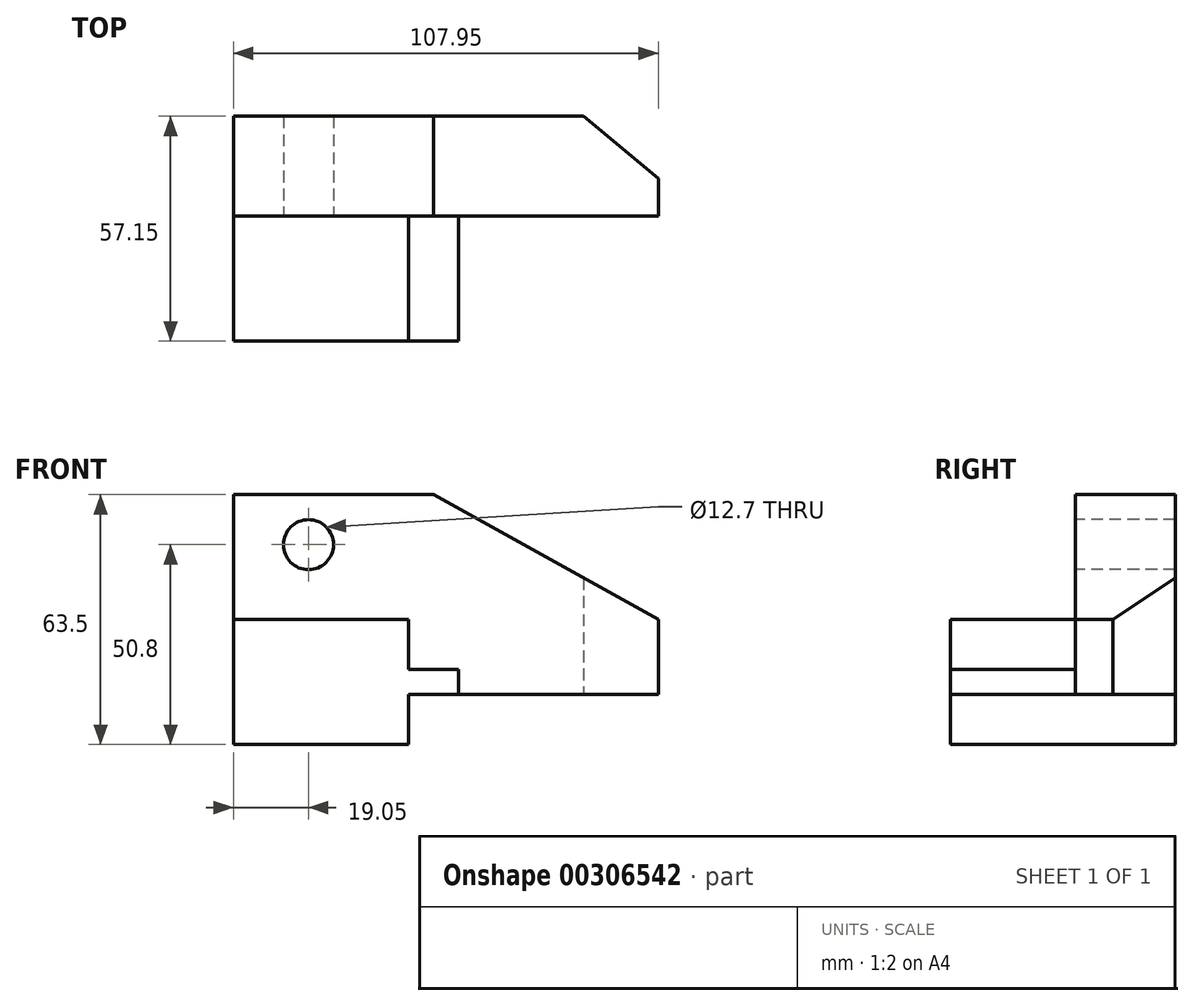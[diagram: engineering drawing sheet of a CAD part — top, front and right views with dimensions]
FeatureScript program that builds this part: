
annotation { "Feature Type Name" : "Feature", "Feature Type Description" : "" }
export const myFeature = defineFeature(function(context is Context, id is Id, definition is map)
    precondition{}
    {
        {
            var Q0;
            Q0=qCreatedBy(makeId("Front.planeOp"),FACE);
            var sketch = newSketch(context, id + "F0", { "sketchPlane" : qUnion([Q0])});
            skLineSegment(sketch, "E0.bottom", {"start": v(0, 0) * mm, "end": v(107.95, 0) * mm});
            skLineSegment(sketch, "E0.top", {"start": v(0, 63.5) * mm, "end": v(107.95, 63.5) * mm});
            skLineSegment(sketch, "E0.left", {"start": v(0, 0) * mm, "end": v(0, 63.5) * mm});
            skLineSegment(sketch, "E0.right", {"start": v(107.95, 0) * mm, "end": v(107.95, 63.5) * mm});
            skSolve(sketch);
        }
        {
            var Q0;
            Q0 = qSketchRegion(id + "F0", true);
            extrude(context, id + "F1", {"entities" : qUnion([Q0]), "oppositeDirection" : true, "depth" : 57.15 * mm});
        }
        {
            var Q0;
            Q0=makeQuery(id+"F1.opExtrude","CAP_FACE",FACE,{"disambiguationData":[OSD([sQuery(id+"F0.wireOp",EDGE,"E0.bottom"),sQuery(id+"F0.wireOp",EDGE,"E0.top"),sQuery(id+"F0.wireOp",EDGE,"E0.left"),sQuery(id+"F0.wireOp",EDGE,"E0.right")])],"isStart":true});
            var sketch = newSketch(context, id + "F2", { "sketchPlane" : qUnion([Q0])});
            skLineSegment(sketch, "E1.top", {"start": v(0, 31.75) * mm, "end": v(44.45, 31.75) * mm});
            skLineSegment(sketch, "E2", {"start": v(44.45, 31.75) * mm, "end": v(44.45, 19.05) * mm});
            skLineSegment(sketch, "E3", {"start": v(44.45, 19.05) * mm, "end": v(57.15, 19.05) * mm});
            skLineSegment(sketch, "E4", {"start": v(57.15, 19.05) * mm, "end": v(57.15, 12.7) * mm});
            skLineSegment(sketch, "E5", {"start": v(57.15, 12.7) * mm, "end": v(44.45, 12.7) * mm});
            skLineSegment(sketch, "E6", {"start": v(44.45, 12.7) * mm, "end": v(44.45, 0) * mm});
            skLineSegment(sketch, "E7", {"start": v(0, 31.75) * mm, "end": v(0, 63.5) * mm});
            skLineSegment(sketch, "E8", {"start": v(0, 63.5) * mm, "end": v(107.95, 63.5) * mm});
            skLineSegment(sketch, "E9", {"start": v(107.95, 63.5) * mm, "end": v(107.95, 0) * mm});
            skLineSegment(sketch, "E10", {"start": v(107.95, 0) * mm, "end": v(44.45, 0) * mm});
            skSolve(sketch);
        }
        {
            var Q0;
            Q0 = qSketchRegion(id + "F2", true);
            extrude(context, id + "F3", {"entities" : qUnion([Q0]), "operationType" : NewBodyOperationType.REMOVE, "oppositeDirection" : true, "depth" : 31.75 * mm});
        }
        {
            var Q0;
            Q0=makeQuery(id+"F3.boolean.opBoolean","COPY",FACE,{"derivedFrom":makeQuery(id+"F3.opExtrude","CAP_FACE",FACE,{"disambiguationData":[OSD([sQuery(id+"F2.wireOp",EDGE,"E1.top"),sQuery(id+"F2.wireOp",EDGE,"E2"),sQuery(id+"F2.wireOp",EDGE,"E3"),sQuery(id+"F2.wireOp",EDGE,"E4"),sQuery(id+"F2.wireOp",EDGE,"E5"),sQuery(id+"F2.wireOp",EDGE,"E6"),sQuery(id+"F2.wireOp",EDGE,"E7"),sQuery(id+"F2.wireOp",EDGE,"E8"),sQuery(id+"F2.wireOp",EDGE,"E9"),sQuery(id+"F2.wireOp",EDGE,"E10")])],"isStart":false})});
            var sketch = newSketch(context, id + "F4", { "sketchPlane" : qUnion([Q0])});
            skLineSegment(sketch, "E11.bottom", {"start": v(44.45, 12.7) * mm, "end": v(107.95, 12.7) * mm});
            skLineSegment(sketch, "E11.top", {"start": v(44.45, 0) * mm, "end": v(107.95, 0) * mm});
            skLineSegment(sketch, "E11.left", {"start": v(44.45, 12.7) * mm, "end": v(44.45, 0) * mm});
            skLineSegment(sketch, "E11.right", {"start": v(107.95, 12.7) * mm, "end": v(107.95, 0) * mm});
            skSolve(sketch);
        }
        {
            var Q0;
            Q0 = qSketchRegion(id + "F4", true);
            extrude(context, id + "F5", {"entities" : qUnion([Q0]), "operationType" : NewBodyOperationType.REMOVE, "endBound" : BoundingType.THROUGH_ALL, "oppositeDirection" : true, "depth" : 25.4 * mm});
        }
        {
            var Q0;
            Q0=makeQuery(id+"F3.boolean.opBoolean","COPY",FACE,{"derivedFrom":makeQuery(id+"F3.opExtrude","CAP_FACE",FACE,{"disambiguationData":[OSD([sQuery(id+"F2.wireOp",EDGE,"E1.top"),sQuery(id+"F2.wireOp",EDGE,"E2"),sQuery(id+"F2.wireOp",EDGE,"E3"),sQuery(id+"F2.wireOp",EDGE,"E4"),sQuery(id+"F2.wireOp",EDGE,"E5"),sQuery(id+"F2.wireOp",EDGE,"E6"),sQuery(id+"F2.wireOp",EDGE,"E7"),sQuery(id+"F2.wireOp",EDGE,"E8"),sQuery(id+"F2.wireOp",EDGE,"E9"),sQuery(id+"F2.wireOp",EDGE,"E10")])],"isStart":false})});
            var sketch = newSketch(context, id + "F6", { "sketchPlane" : qUnion([Q0])});
            skLineSegment(sketch, "E12", {"start": v(107.95, 12.7) * mm, "end": v(107.95, 31.75) * mm});
            skLineSegment(sketch, "E13", {"start": v(107.95, 31.75) * mm, "end": v(50.8, 63.5) * mm});
            skLineSegment(sketch, "E14", {"start": v(50.8, 63.5) * mm, "end": v(107.95, 63.5) * mm});
            skLineSegment(sketch, "E15", {"start": v(107.95, 63.5) * mm, "end": v(107.95, 31.75) * mm});
            skSolve(sketch);
        }
        {
            var Q0;
            Q0 = qSketchRegion(id + "F6", true);
            extrude(context, id + "F7", {"entities" : qUnion([Q0]), "operationType" : NewBodyOperationType.REMOVE, "endBound" : BoundingType.THROUGH_ALL, "oppositeDirection" : true, "depth" : 25.4 * mm});
        }
        {
            var Q0;
            Q0=makeQuery(id+"F3.boolean.opBoolean","COPY",FACE,{"derivedFrom":makeQuery(id+"F3.opExtrude","CAP_FACE",FACE,{"disambiguationData":[OSD([sQuery(id+"F2.wireOp",EDGE,"E1.top"),sQuery(id+"F2.wireOp",EDGE,"E2"),sQuery(id+"F2.wireOp",EDGE,"E3"),sQuery(id+"F2.wireOp",EDGE,"E4"),sQuery(id+"F2.wireOp",EDGE,"E5"),sQuery(id+"F2.wireOp",EDGE,"E6"),sQuery(id+"F2.wireOp",EDGE,"E7"),sQuery(id+"F2.wireOp",EDGE,"E8"),sQuery(id+"F2.wireOp",EDGE,"E9"),sQuery(id+"F2.wireOp",EDGE,"E10")])],"isStart":false})});
            var sketch = newSketch(context, id + "F8", { "sketchPlane" : qUnion([Q0])});
            skLineSegment(sketch, "E16", {"start": v(0, 50.8) * mm, "end": v(19.05, 50.8) * mm});
            skCircle(sketch, "E17", {"center": v(19.05, 50.8) * mm, "radius": 6.35 * mm});
            skSolve(sketch);
        }
        {
            var Q0;
            Q0 = qSketchRegion(id + "F8", true);
            extrude(context, id + "F9", {"entities" : qUnion([Q0]), "operationType" : NewBodyOperationType.REMOVE, "endBound" : BoundingType.THROUGH_ALL, "oppositeDirection" : true, "depth" : 25.4 * mm});
        }
        {
            var Q0;
            Q0=makeQuery(id+"F5.boolean.opBoolean","MERGE",FACE,{"derivedFrom":[makeQuery(id+"F3.boolean.opBoolean","COPY",FACE,{"derivedFrom":makeQuery(id+"F3.opExtrude","SWEPT_FACE",FACE,{"disambiguationData":[OSD([sQuery(id+"F2.wireOp",EDGE,"E5")])]})}),makeQuery(id+"F5.opExtrude","SWEPT_FACE",FACE,{"disambiguationData":[OSD([sQuery(id+"F4.wireOp",EDGE,"E11.bottom")])]})]});
            var sketch = newSketch(context, id + "F10", { "sketchPlane" : qUnion([Q0])});
            skLineSegment(sketch, "E18", {"start": v(107.95, -31.75) * mm, "end": v(107.95, -41.27) * mm});
            skLineSegment(sketch, "E19", {"start": v(107.95, -31.75) * mm, "end": v(88.9, -31.75) * mm});
            skLineSegment(sketch, "E20", {"start": v(107.95, -41.28) * mm, "end": v(88.9, -57.15) * mm});
            skLineSegment(sketch, "E21", {"start": v(107.95, -41.27) * mm, "end": v(107.95, -57.15) * mm});
            skLineSegment(sketch, "E22", {"start": v(107.95, -57.15) * mm, "end": v(88.9, -57.15) * mm});
            skSolve(sketch);
        }
        {
            var Q0;
            Q0 = qSketchRegion(id + "F10", true);
            extrude(context, id + "F11", {"entities" : qUnion([Q0]), "operationType" : NewBodyOperationType.REMOVE, "endBound" : BoundingType.THROUGH_ALL, "oppositeDirection" : true, "depth" : 25.4 * mm});
        }
    });
